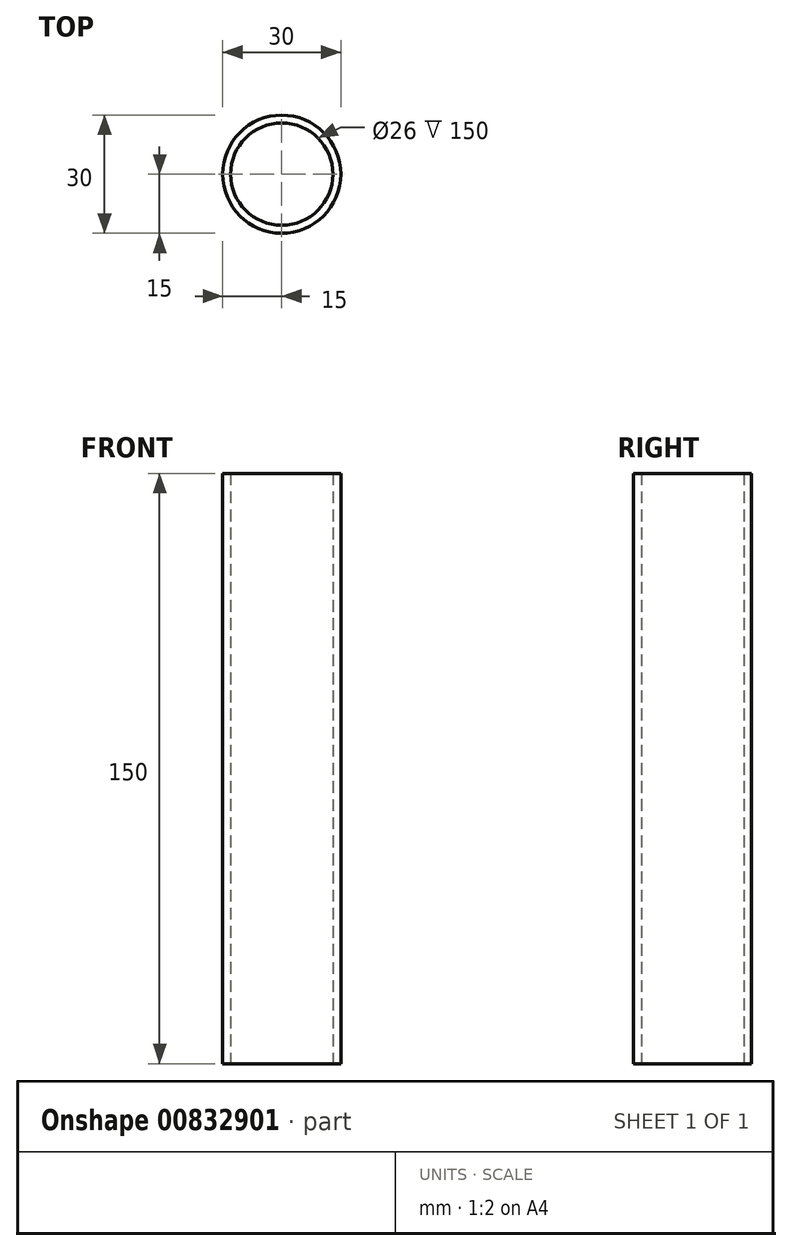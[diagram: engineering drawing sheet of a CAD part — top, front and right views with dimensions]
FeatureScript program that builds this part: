
annotation { "Feature Type Name" : "Feature", "Feature Type Description" : "" }
export const myFeature = defineFeature(function(context is Context, id is Id, definition is map)
    precondition{}
    {
        {
            var Q0;
            Q0=qCreatedBy(makeId("Top.planeOp"),FACE);
            var sketch = newSketch(context, id + "F0", { "sketchPlane" : qUnion([Q0])});
            skCircle(sketch, "E0", {"center": v(0, 0) * mm, "radius": 15 * mm});
            skCircle(sketch, "E1.0", {"center": v(0, 0) * mm, "radius": 13 * mm});
            skSolve(sketch);
        }
        {
            var Q0;
            Q0=makeQuery(id+"F0.imprint","IMPRINT",FACE,{"disambiguationData":[TD([[makeQuery(id+"F0.imprint","IMPRINT",EDGE,{"derivedFrom":sQuery(id+"F0.wireOp",EDGE,"E0")}),1.0]])]});
            extrude(context, id + "F1", {"entities" : qUnion([Q0]), "depth" : 150 * mm, "offsetDistance" : 25 * mm});
        }
        {
            var Q0;
            Q0=qCreatedBy(makeId("Top.planeOp"),FACE);
            var sketch = newSketch(context, id + "F2", { "sketchPlane" : qUnion([Q0])});
            skLineSegment(sketch, "E2", {"start": v(0, 34.43) * mm, "end": v(0, -48.05) * mm});
            skSolve(sketch);
        }
        {
            var Q0;
            Q0=qCreatedBy(makeId("Top.planeOp"),FACE);
            var Q1;
            Q1=sQuery(id+"F2.wireOp",EDGE,"E2");
            cPlane(context, id + "F3", {"entities" : qUnion([Q0, Q1]), "cplaneType" : CPlaneType.LINE_ANGLE, "offset" : 25 * mm, "angle" : 45 * degree, "oppositeDirection" : true, "width" : 150 * mm, "height" : 150 * mm});
        }
        {
            var Q0;
            Q0=qCreatedBy(id+"F3.planeOp",FACE);
            var sketch = newSketch(context, id + "F4", { "sketchPlane" : qUnion([Q0])});
            skLineSegment(sketch, "E3.bottom", {"start": v(-31.42, 4) * mm, "end": v(-16.42, 4) * mm});
            skLineSegment(sketch, "E3.top", {"start": v(-31.42, -4) * mm, "end": v(-16.42, -4) * mm});
            skLineSegment(sketch, "E3.left", {"start": v(-31.42, 4) * mm, "end": v(-31.42, -4) * mm});
            skLineSegment(sketch, "E3.right", {"start": v(-16.42, 4) * mm, "end": v(-16.42, -4) * mm});
            skSolve(sketch);
        }
        {
            var Q0;
            Q0=makeQuery(id+"F4.imprint","IMPRINT",FACE,{"disambiguationData":[TD([[makeQuery(id+"F4.imprint","IMPRINT",EDGE,{"derivedFrom":sQuery(id+"F4.wireOp",EDGE,"E3.bottom")}),-1.0]])]});
            extrude(context, id + "F5", {"entities" : qUnion([Q0]), "operationType" : NewBodyOperationType.ADD, "oppositeDirection" : true, "depth" : 200 * mm, "offsetDistance" : 25 * mm});
        }
        {
            var Q0;
            Q0=makeQuery(id+"F1.opExtrude","SWEPT_BODY",BODY,{"disambiguationData":[OSD([sQuery(id+"F0.wireOp",EDGE,"E0"),sQuery(id+"F0.wireOp",EDGE,"E1.0")])]});
            var Q1;
            Q1=makeQuery(id+"F5.opExtrude","SWEPT_BODY",BODY,{"disambiguationData":[OSD([sQuery(id+"F4.wireOp",EDGE,"E3.bottom"),sQuery(id+"F4.wireOp",EDGE,"E3.top"),sQuery(id+"F4.wireOp",EDGE,"E3.left"),sQuery(id+"F4.wireOp",EDGE,"E3.right")])]});
            booleanBodies(context, id + "F6", {"operationType" : BooleanOperationType.SUBTRACTION, "tools" : qUnion([Q0]), "targets" : qUnion([Q1]), "keepTools" : true});
        }
        {
            var Q0;
            Q0=makeQuery(id+"F6.opBoolean","SPLIT",BODY,{"disambiguationData":[OD(2.0)],"derivedFrom":makeQuery(id+"F5.opExtrude","SWEPT_BODY",BODY,{"disambiguationData":[OSD([sQuery(id+"F4.wireOp",EDGE,"E3.bottom"),sQuery(id+"F4.wireOp",EDGE,"E3.top"),sQuery(id+"F4.wireOp",EDGE,"E3.left"),sQuery(id+"F4.wireOp",EDGE,"E3.right")])]})});
            var Q1;
            Q1=makeQuery(id+"F6.opBoolean","SPLIT",BODY,{"disambiguationData":[OD(0.0)],"derivedFrom":makeQuery(id+"F5.opExtrude","SWEPT_BODY",BODY,{"disambiguationData":[OSD([sQuery(id+"F4.wireOp",EDGE,"E3.bottom"),sQuery(id+"F4.wireOp",EDGE,"E3.top"),sQuery(id+"F4.wireOp",EDGE,"E3.left"),sQuery(id+"F4.wireOp",EDGE,"E3.right")])]})});
            deleteBodies(context, id + "F7", {"entities" : qUnion([Q0, Q1])});
        }
    });
